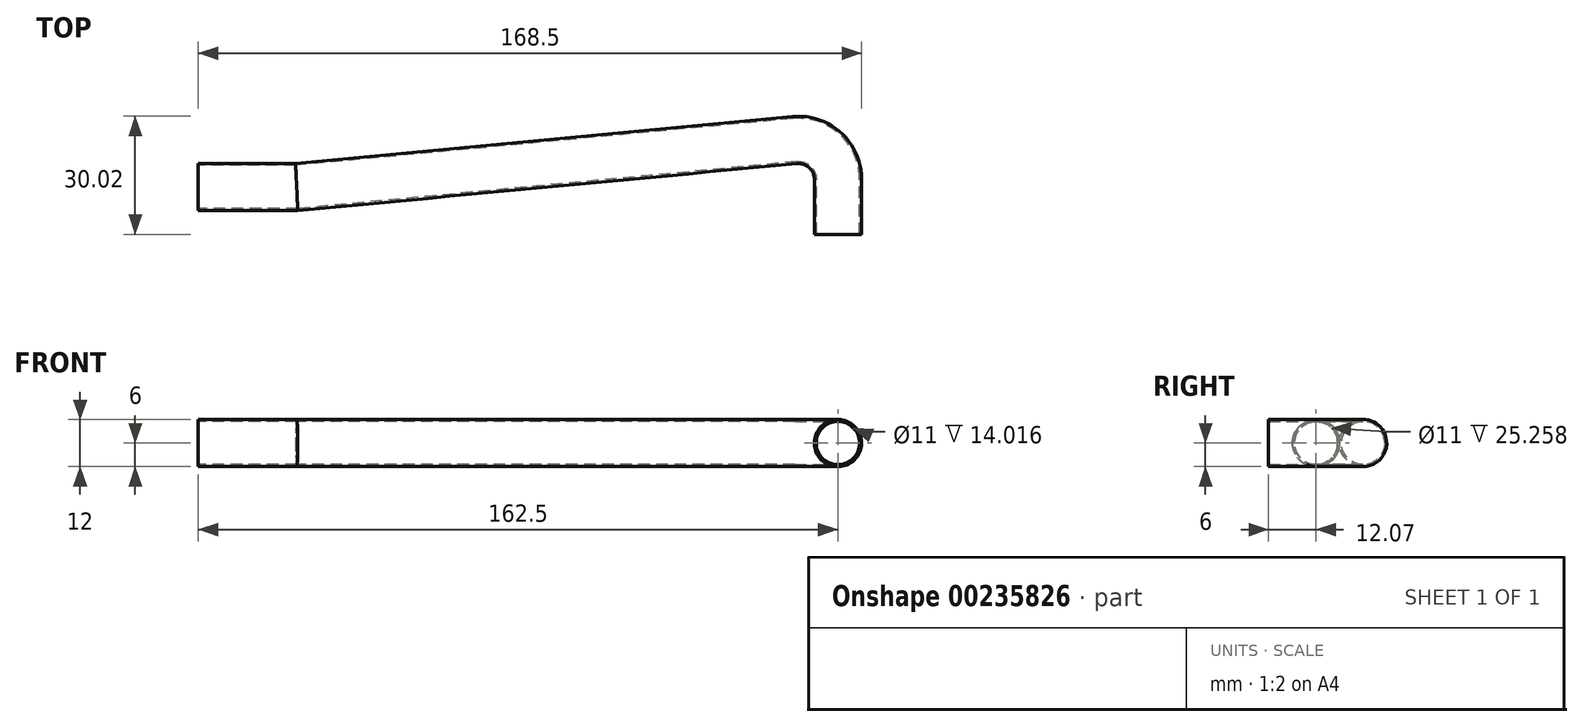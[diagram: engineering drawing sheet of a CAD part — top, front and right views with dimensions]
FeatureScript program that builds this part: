
annotation { "Feature Type Name" : "Feature", "Feature Type Description" : "" }
export const myFeature = defineFeature(function(context is Context, id is Id, definition is map)
    precondition{}
    {
        {
            var Q0;
            Q0=qCreatedBy(makeId("Front.planeOp"),FACE);
            var sketch = newSketch(context, id + "F0", { "sketchPlane" : qUnion([Q0])});
            skCircle(sketch, "E0", {"center": v(0, 0) * mm, "radius": 6 * mm});
            skSolve(sketch);
        }
        {
            var Q0;
            Q0=qCreatedBy(makeId("Top.planeOp"),FACE);
            var sketch = newSketch(context, id + "F1", { "sketchPlane" : qUnion([Q0])});
            skLineSegment(sketch, "E1", {"start": v(0, 0) * mm, "end": v(0, 14.02) * mm});
            skLineSegment(sketch, "E2", {"start": v(-162.5, 12.07) * mm, "end": v(-137.5, 12.07) * mm});
            skLineSegment(sketch, "E3", {"start": v(-137.5, 12.07) * mm, "end": v(-10.94, 23.97) * mm});
            skPoint(sketch, "E4.visualSharp", {"position": v(0, 25) * mm});
            skArc(sketch, "E4.filletArc", {"start": v(0, 14.02) * mm, "mid": v(-3.27, 21.41) * mm, "end": v(-10.94, 23.97) * mm});
            skSolve(sketch);
        }
        {
            var Q0;
            Q0=makeQuery(id+"F0.imprint","IMPRINT",FACE,{"disambiguationData":[TD([[makeQuery(id+"F0.imprint","IMPRINT",EDGE,{"derivedFrom":sQuery(id+"F0.wireOp",EDGE,"E0")}),1.0]])]});
            var Q1;
            Q1=sQuery(id+"F1.wireOp",EDGE,"E2");
            var Q2;
            Q2=sQuery(id+"F1.wireOp",EDGE,"E3");
            var Q3;
            Q3=sQuery(id+"F1.wireOp",EDGE,"E4.filletArc");
            var Q4;
            Q4=sQuery(id+"F1.wireOp",EDGE,"E1");
            sweep(context, id + "F2", {"profiles" : qUnion([Q0]), "path" : qUnion([Q1, Q2, Q3, Q4])});
        }
        {
            var Q0;
            Q0=makeQuery(id+"F2.opSweep","CAP_FACE",FACE,{"disambiguationData":[OSD([sQuery(id+"F0.wireOp",EDGE,"E0"),sQuery(id+"F1.wireOp",VERTEX,"E1.start")])],"isStart":true});
            var Q1;
            Q1=makeQuery(id+"F2.opSweep","CAP_FACE",FACE,{"disambiguationData":[OSD([sQuery(id+"F0.wireOp",EDGE,"E0"),sQuery(id+"F1.wireOp",VERTEX,"E2.start")])],"isStart":false});
            var Q2;
            Q2=makeQuery(id+"F2.opSweep","SWEPT_BODY",BODY,{"disambiguationData":[OSD([sQuery(id+"F0.wireOp",EDGE,"E0"),sQuery(id+"F1.wireOp",EDGE,"E1")])]});
            shell(context, id + "F3", {"entities" : qUnion([Q0, Q1]), "parts" : qUnion([Q2]), "thickness" : .5 * mm});
        }
    });
